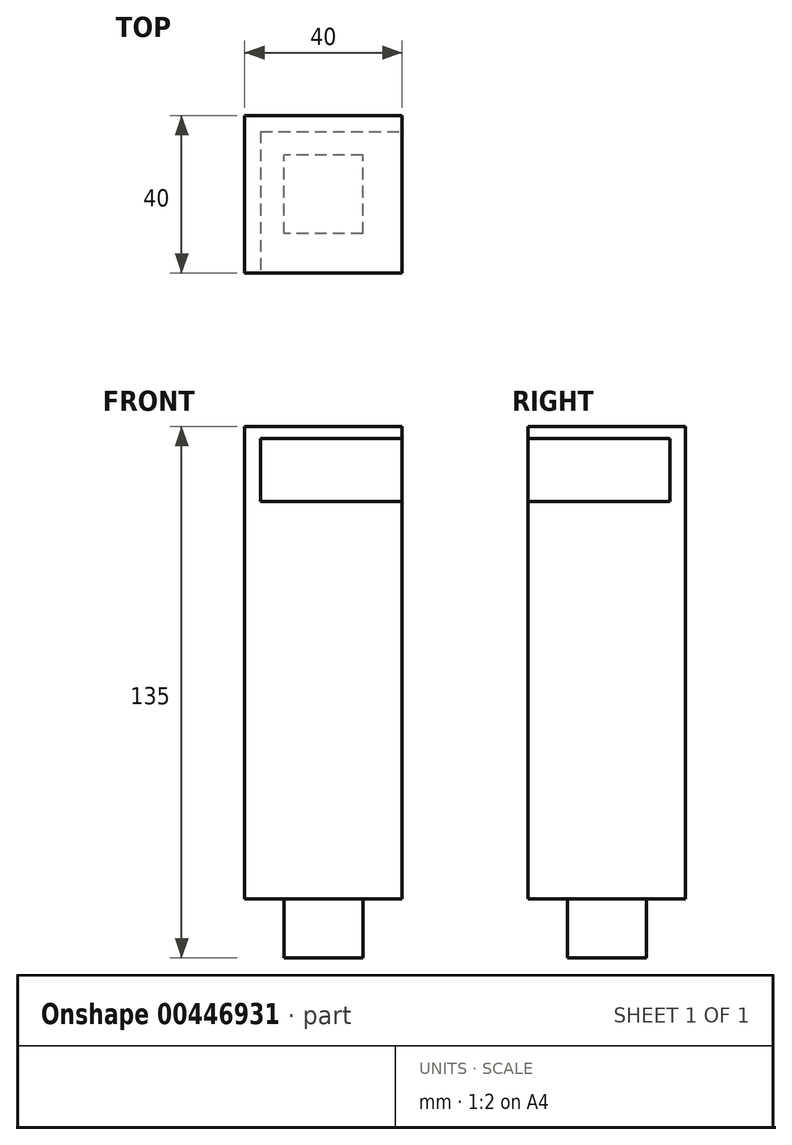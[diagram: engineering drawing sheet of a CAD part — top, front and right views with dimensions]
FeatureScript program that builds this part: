
annotation { "Feature Type Name" : "Feature", "Feature Type Description" : "" }
export const myFeature = defineFeature(function(context is Context, id is Id, definition is map)
    precondition{}
    {
        {
            var Q0;
            Q0=qCreatedBy(makeId("Top.planeOp"),FACE);
            var sketch = newSketch(context, id + "F0", { "sketchPlane" : qUnion([Q0])});
            skLineSegment(sketch, "E0.bottom", {"start": v(20, 20) * mm, "end": v(-20, 20) * mm});
            skLineSegment(sketch, "E0.top", {"start": v(20, -20) * mm, "end": v(-20, -20) * mm});
            skLineSegment(sketch, "E0.left", {"start": v(20, 20) * mm, "end": v(20, -20) * mm});
            skLineSegment(sketch, "E0.right", {"start": v(-20, 20) * mm, "end": v(-20, -20) * mm});
            skPoint(sketch, "E0.middle", {"position": v(0, 0) * mm});
            skSolve(sketch);
        }
        {
            var Q0;
            Q0=makeQuery(id+"F0.imprint","IMPRINT",FACE,{"disambiguationData":[TD([[makeQuery(id+"F0.imprint","IMPRINT",EDGE,{"derivedFrom":sQuery(id+"F0.wireOp",EDGE,"E0.bottom")}),1.0]])]});
            extrude(context, id + "F1", {"entities" : qUnion([Q0]), "depth" : 120 * mm});
        }
        {
            var Q0;
            Q0=makeQuery(id+"F1.opExtrude","SWEPT_FACE",FACE,{"disambiguationData":[OSD([sQuery(id+"F0.wireOp",EDGE,"E0.top")])]});
            var sketch = newSketch(context, id + "F2", { "sketchPlane" : qUnion([Q0])});
            skLineSegment(sketch, "E1.bottom", {"start": v(-16, 117) * mm, "end": v(20, 117) * mm});
            skLineSegment(sketch, "E1.top", {"start": v(-16, 101) * mm, "end": v(20, 101) * mm});
            skLineSegment(sketch, "E1.left", {"start": v(-16, 117) * mm, "end": v(-16, 101) * mm});
            skLineSegment(sketch, "E1.right", {"start": v(20, 117) * mm, "end": v(20, 101) * mm});
            skSolve(sketch);
        }
        {
            var Q0;
            Q0 = qSketchRegion(id + "F2", true);
            extrude(context, id + "F3", {"entities" : qUnion([Q0]), "operationType" : NewBodyOperationType.REMOVE, "oppositeDirection" : true, "depth" : 36 * mm});
        }
        {
            var Q0;
            Q0=makeQuery(id+"F1.opExtrude","CAP_FACE",FACE,{"disambiguationData":[OSD([sQuery(id+"F0.wireOp",EDGE,"E0.bottom"),sQuery(id+"F0.wireOp",EDGE,"E0.top"),sQuery(id+"F0.wireOp",EDGE,"E0.left"),sQuery(id+"F0.wireOp",EDGE,"E0.right")])],"isStart":true});
            var sketch = newSketch(context, id + "F4", { "sketchPlane" : qUnion([Q0])});
            skLineSegment(sketch, "E2.bottom", {"start": v(10, 10) * mm, "end": v(-10, 10) * mm});
            skLineSegment(sketch, "E2.top", {"start": v(10, -10) * mm, "end": v(-10, -10) * mm});
            skLineSegment(sketch, "E2.left", {"start": v(10, 10) * mm, "end": v(10, -10) * mm});
            skLineSegment(sketch, "E2.right", {"start": v(-10, 10) * mm, "end": v(-10, -10) * mm});
            skPoint(sketch, "E2.middle", {"position": v(0, 0) * mm});
            skSolve(sketch);
        }
        {
            var Q0;
            Q0 = qSketchRegion(id + "F4", true);
            extrude(context, id + "F5", {"entities" : qUnion([Q0]), "operationType" : NewBodyOperationType.ADD, "depth" : 15 * mm});
        }
    });
